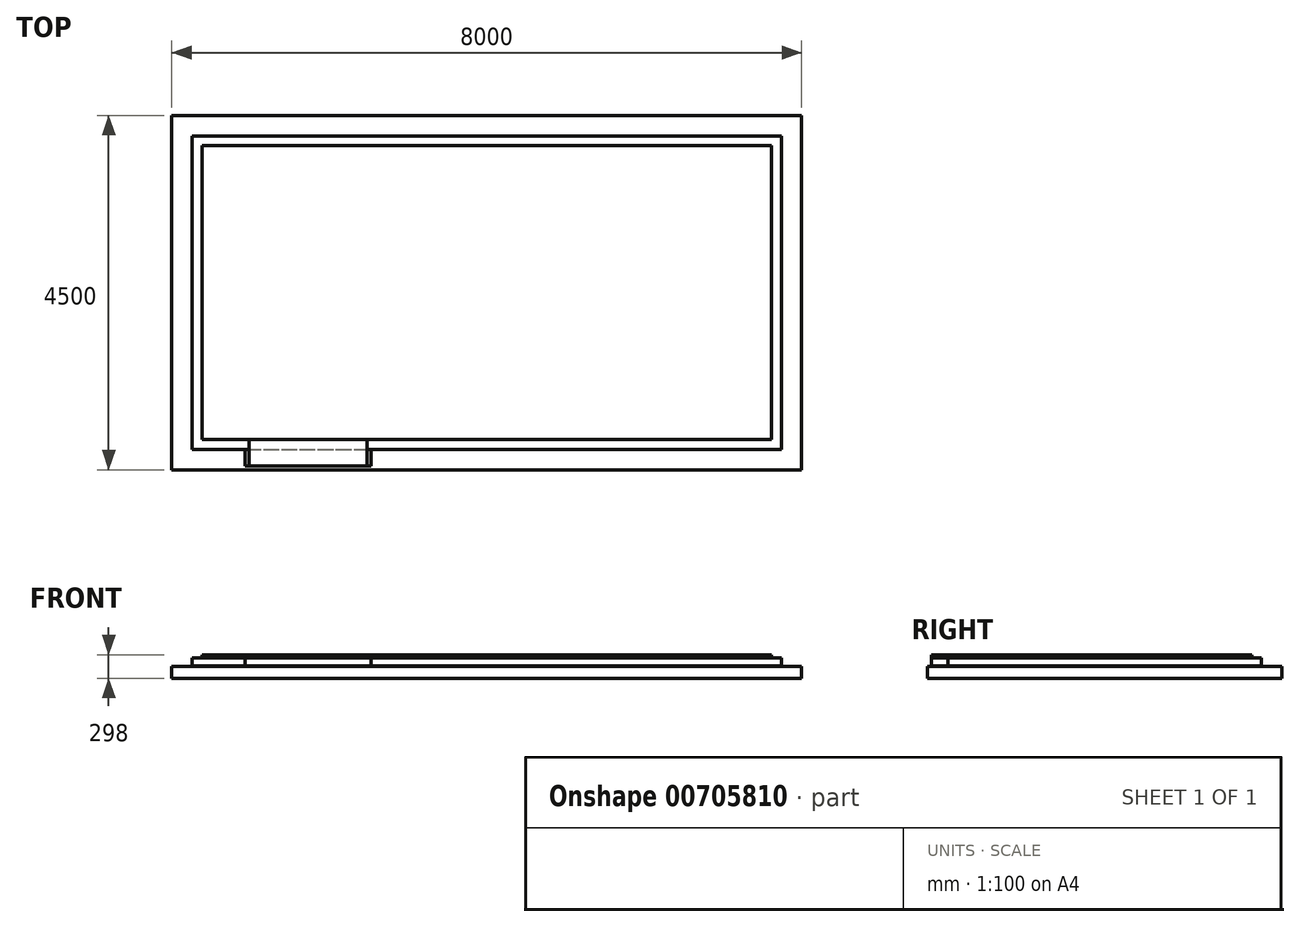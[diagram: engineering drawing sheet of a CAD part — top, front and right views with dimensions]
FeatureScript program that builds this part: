
annotation { "Feature Type Name" : "Feature", "Feature Type Description" : "" }
export const myFeature = defineFeature(function(context is Context, id is Id, definition is map)
    precondition{}
    {
        {
            var Q0;
            Q0=qCreatedBy(makeId("Top.planeOp"),FACE);
            var sketch = newSketch(context, id + "F0", { "sketchPlane" : qUnion([Q0])});
            skLineSegment(sketch, "E0.bottom", {"start": v(-98.14, -34.97) * mm, "end": v(7901.86, -34.97) * mm});
            skLineSegment(sketch, "E0.top", {"start": v(-98.14, 4465.03) * mm, "end": v(7901.86, 4465.03) * mm});
            skLineSegment(sketch, "E0.left", {"start": v(-98.14, -34.97) * mm, "end": v(-98.14, 4465.03) * mm});
            skLineSegment(sketch, "E0.right", {"start": v(7901.86, -34.97) * mm, "end": v(7901.86, 4465.03) * mm});
            skSolve(sketch);
        }
        {
            var Q0;
            Q0=makeQuery(id+"F0.imprint","IMPRINT",FACE,{"disambiguationData":[TD([[makeQuery(id+"F0.imprint","IMPRINT",EDGE,{"derivedFrom":sQuery(id+"F0.wireOp",EDGE,"E0.bottom")}),1.0]])]});
            extrude(context, id + "F1", {"entities" : qUnion([Q0]), "depth" : 150 * mm, "offsetDistance" : 25 * mm});
        }
        {
            var Q0;
            Q0=makeQuery(id+"F1.opExtrude","CAP_FACE",FACE,{"disambiguationData":[OSD([sQuery(id+"F0.wireOp",EDGE,"E0.bottom"),sQuery(id+"F0.wireOp",EDGE,"E0.top"),sQuery(id+"F0.wireOp",EDGE,"E0.left"),sQuery(id+"F0.wireOp",EDGE,"E0.right")])],"isStart":false});
            var sketch = newSketch(context, id + "F2", { "sketchPlane" : qUnion([Q0])});
            skLineSegment(sketch, "E1.bottom", {"start": v(159.86, 223.03) * mm, "end": v(7643.86, 223.03) * mm});
            skLineSegment(sketch, "E1.top", {"start": v(159.86, 4207.03) * mm, "end": v(7643.86, 4207.03) * mm});
            skLineSegment(sketch, "E1.left", {"start": v(159.86, 223.03) * mm, "end": v(159.86, 4207.03) * mm});
            skLineSegment(sketch, "E1.right", {"start": v(7643.86, 223.03) * mm, "end": v(7643.86, 4207.03) * mm});
            skSolve(sketch);
        }
        {
            var Q0;
            Q0=makeQuery(id+"F2.imprint","IMPRINT",FACE,{"disambiguationData":[TD([[makeQuery(id+"F2.imprint","IMPRINT",EDGE,{"derivedFrom":sQuery(id+"F2.wireOp",EDGE,"E1.bottom")}),1.0]])]});
            extrude(context, id + "F3", {"entities" : qUnion([Q0]), "depth" : 8 * mm, "offsetDistance" : 25 * mm});
        }
        {
            var Q0;
            Q0=makeQuery(id+"F3.opExtrude","SWEPT_FACE",FACE,{"disambiguationData":[OSD([sQuery(id+"F2.wireOp",EDGE,"E1.bottom")])]});
            var sketch = newSketch(context, id + "F4", { "sketchPlane" : qUnion([Q0])});
            skLineSegment(sketch, "E2.bottom", {"start": v(834.86, 158) * mm, "end": v(2434.86, 158) * mm});
            skLineSegment(sketch, "E2.top", {"start": v(834.86, 150) * mm, "end": v(2434.86, 150) * mm});
            skLineSegment(sketch, "E2.left", {"start": v(834.86, 158) * mm, "end": v(834.86, 150) * mm});
            skLineSegment(sketch, "E2.right", {"start": v(2434.86, 158) * mm, "end": v(2434.86, 150) * mm});
            skSolve(sketch);
        }
        {
            var Q0;
            Q0=makeQuery(id+"F4.imprint","IMPRINT",FACE,{"disambiguationData":[TD([[makeQuery(id+"F4.imprint","IMPRINT",EDGE,{"derivedFrom":sQuery(id+"F4.wireOp",EDGE,"E2.bottom")}),-1.0]])]});
            extrude(context, id + "F5", {"entities" : qUnion([Q0]), "depth" : 201 * mm, "offsetDistance" : 25 * mm});
        }
        {
            var Q0;
            Q0=makeQuery(id+"F3.opExtrude","CAP_FACE",FACE,{"disambiguationData":[OSD([sQuery(id+"F2.wireOp",EDGE,"E1.bottom"),sQuery(id+"F2.wireOp",EDGE,"E1.top"),sQuery(id+"F2.wireOp",EDGE,"E1.left"),sQuery(id+"F2.wireOp",EDGE,"E1.right")])],"isStart":false});
            var sketch = newSketch(context, id + "F6", { "sketchPlane" : qUnion([Q0])});
            skLineSegment(sketch, "E3.bottom", {"start": v(159.86, 223.03) * mm, "end": v(7643.86, 223.03) * mm});
            skLineSegment(sketch, "E3.top", {"start": v(159.86, 4207.03) * mm, "end": v(7643.86, 4207.03) * mm});
            skLineSegment(sketch, "E3.left", {"start": v(159.86, 223.03) * mm, "end": v(159.86, 4207.03) * mm});
            skLineSegment(sketch, "E3.right", {"start": v(7643.86, 223.03) * mm, "end": v(7643.86, 4207.03) * mm});
            skSolve(sketch);
        }
        {
            var Q0;
            Q0=makeQuery(id+"F6.imprint","IMPRINT",FACE,{"disambiguationData":[TD([[makeQuery(id+"F6.imprint","IMPRINT",EDGE,{"derivedFrom":sQuery(id+"F6.wireOp",EDGE,"E3.bottom")}),1.0]])]});
            extrude(context, id + "F7", {"entities" : qUnion([Q0]), "depth" : 100 * mm, "offsetDistance" : 25 * mm});
        }
        {
            var Q0;
            Q0=makeQuery(id+"F7.opExtrude","SWEPT_FACE",FACE,{"disambiguationData":[OSD([sQuery(id+"F6.wireOp",EDGE,"E3.bottom")])]});
            var sketch = newSketch(context, id + "F8", { "sketchPlane" : qUnion([Q0])});
            skLineSegment(sketch, "E4.bottom", {"start": v(834.86, 258) * mm, "end": v(2434.86, 258) * mm});
            skLineSegment(sketch, "E4.top", {"start": v(834.86, 158) * mm, "end": v(2434.86, 158) * mm});
            skLineSegment(sketch, "E4.left", {"start": v(834.86, 258) * mm, "end": v(834.86, 158) * mm});
            skLineSegment(sketch, "E4.right", {"start": v(2434.86, 258) * mm, "end": v(2434.86, 158) * mm});
            skSolve(sketch);
        }
        {
            var Q0;
            Q0=makeQuery(id+"F8.imprint","IMPRINT",FACE,{"disambiguationData":[TD([[makeQuery(id+"F8.imprint","IMPRINT",EDGE,{"derivedFrom":sQuery(id+"F8.wireOp",EDGE,"E4.bottom")}),-1.0]])]});
            extrude(context, id + "F9", {"entities" : qUnion([Q0]), "depth" : 209 * mm, "offsetDistance" : 25 * mm});
        }
        {
            var Q0;
            Q0=makeQuery(id+"F7.opExtrude","CAP_FACE",FACE,{"disambiguationData":[OSD([sQuery(id+"F6.wireOp",EDGE,"E3.bottom"),sQuery(id+"F6.wireOp",EDGE,"E3.top"),sQuery(id+"F6.wireOp",EDGE,"E3.left"),sQuery(id+"F6.wireOp",EDGE,"E3.right")])],"isStart":false});
            var sketch = newSketch(context, id + "F10", { "sketchPlane" : qUnion([Q0])});
            skLineSegment(sketch, "E5.bottom", {"start": v(284.86, 4082.03) * mm, "end": v(7518.86, 4082.03) * mm});
            skLineSegment(sketch, "E5.top", {"start": v(284.86, 348.03) * mm, "end": v(7518.86, 348.03) * mm});
            skLineSegment(sketch, "E5.left", {"start": v(284.86, 4082.03) * mm, "end": v(284.86, 348.03) * mm});
            skLineSegment(sketch, "E5.right", {"start": v(7518.86, 4082.03) * mm, "end": v(7518.86, 348.03) * mm});
            skSolve(sketch);
        }
        {
            var Q0;
            Q0=makeQuery(id+"F10.imprint","IMPRINT",FACE,{"disambiguationData":[TD([[makeQuery(id+"F10.imprint","IMPRINT",EDGE,{"derivedFrom":sQuery(id+"F10.wireOp",EDGE,"E5.bottom")}),-1.0]])]});
            extrude(context, id + "F11", {"entities" : qUnion([Q0]), "depth" : 22 * mm, "offsetDistance" : 25 * mm});
        }
        {
            var Q0;
            Q0=makeQuery(id+"F11.opExtrude","SWEPT_FACE",FACE,{"disambiguationData":[OSD([sQuery(id+"F10.wireOp",EDGE,"E5.top")])]});
            var sketch = newSketch(context, id + "F12", { "sketchPlane" : qUnion([Q0])});
            skLineSegment(sketch, "E6.bottom", {"start": v(884.86, 280) * mm, "end": v(2384.86, 280) * mm});
            skLineSegment(sketch, "E6.top", {"start": v(884.86, 258) * mm, "end": v(2384.86, 258) * mm});
            skLineSegment(sketch, "E6.left", {"start": v(884.86, 280) * mm, "end": v(884.86, 258) * mm});
            skLineSegment(sketch, "E6.right", {"start": v(2384.86, 280) * mm, "end": v(2384.86, 258) * mm});
            skSolve(sketch);
        }
        {
            var Q0;
            Q0=makeQuery(id+"F12.imprint","IMPRINT",FACE,{"disambiguationData":[TD([[makeQuery(id+"F12.imprint","IMPRINT",EDGE,{"derivedFrom":sQuery(id+"F12.wireOp",EDGE,"E6.bottom")}),-1.0]])]});
            extrude(context, id + "F13", {"entities" : qUnion([Q0]), "depth" : 334 * mm, "offsetDistance" : 25 * mm});
        }
        {
            var Q0;
            Q0=makeQuery(id+"F11.opExtrude","CAP_FACE",FACE,{"disambiguationData":[OSD([sQuery(id+"F10.wireOp",EDGE,"E5.bottom"),sQuery(id+"F10.wireOp",EDGE,"E5.top"),sQuery(id+"F10.wireOp",EDGE,"E5.left"),sQuery(id+"F10.wireOp",EDGE,"E5.right")])],"isStart":false});
            var sketch = newSketch(context, id + "F14", { "sketchPlane" : qUnion([Q0])});
            skLineSegment(sketch, "E7.bottom", {"start": v(284.86, 348.03) * mm, "end": v(7518.86, 348.03) * mm});
            skLineSegment(sketch, "E7.top", {"start": v(284.86, 4082.03) * mm, "end": v(7518.86, 4082.03) * mm});
            skLineSegment(sketch, "E7.left", {"start": v(284.86, 348.03) * mm, "end": v(284.86, 4082.03) * mm});
            skLineSegment(sketch, "E7.right", {"start": v(7518.86, 348.03) * mm, "end": v(7518.86, 4082.03) * mm});
            skSolve(sketch);
        }
        {
            var Q0;
            Q0=makeQuery(id+"F14.imprint","IMPRINT",FACE,{"disambiguationData":[TD([[makeQuery(id+"F14.imprint","IMPRINT",EDGE,{"derivedFrom":sQuery(id+"F14.wireOp",EDGE,"E7.bottom")}),1.0]])]});
            extrude(context, id + "F15", {"entities" : qUnion([Q0]), "depth" : 18 * mm, "offsetDistance" : 25 * mm});
        }
        {
            var Q0;
            Q0=makeQuery(id+"F13.opExtrude","SWEPT_FACE",FACE,{"disambiguationData":[OSD([sQuery(id+"F12.wireOp",EDGE,"E6.bottom")])]});
            var sketch = newSketch(context, id + "F16", { "sketchPlane" : qUnion([Q0])});
            skLineSegment(sketch, "E8.bottom", {"start": v(884.86, 14.03) * mm, "end": v(2384.86, 14.03) * mm});
            skLineSegment(sketch, "E8.top", {"start": v(884.86, 348.03) * mm, "end": v(2384.86, 348.03) * mm});
            skLineSegment(sketch, "E8.left", {"start": v(884.86, 14.03) * mm, "end": v(884.86, 348.03) * mm});
            skLineSegment(sketch, "E8.right", {"start": v(2384.86, 14.03) * mm, "end": v(2384.86, 348.03) * mm});
            skSolve(sketch);
        }
        {
            var Q0;
            Q0=makeQuery(id+"F16.imprint","IMPRINT",FACE,{"disambiguationData":[TD([[makeQuery(id+"F16.imprint","IMPRINT",EDGE,{"derivedFrom":sQuery(id+"F16.wireOp",EDGE,"E8.bottom")}),1.0]])]});
            extrude(context, id + "F17", {"entities" : qUnion([Q0]), "depth" : 18 * mm, "offsetDistance" : 25 * mm});
        }
    });
